# Revit family: Lavatory_System-Free_Standing-Trueform_Concrete-Single_Ramp_Basin-Configurable_2_Station
name_source: partatom
category: Plumbing Fixtures
revit_build: Autodesk Revit LT 2015 (Build: 20140606_1530(x64)
units: mm (PartAtom-declared; Revit-internal decimal feet)

## types (3) — shared parameters
Additional Support Required Note = No
Apron Height = 5"
Base = Steel, Paint Finish, Black, Matte
Basin Depth = 13"
Basin Front Setback = 4"
Basin Front Setback MAX = 7"
Basin Front Setback MIN = 3"
Basin Height = 5"
Basin/Countertop Reconciliation Warning = No
Countertop Height = 34"
Lavatory = GFRC - Concrete
Leveling Feet = Stainless Steel
Manufacturer = Trueform Concrete
Non Standard Sink Basin Model Note = No
Overall Countertop Depth = 22"
Overall Countertop Depth MIN = 18"
Tailpiece = Polished Chrome
URL = https://www.trueformconcrete.com
Vent Connection = No
Verify Basin Front Setback = 4"
Verify Overall Countertop Depth = 22"
Verify Rear Countertop = 5"
WFU = 3
Waste Connection = Yes
Waste Fitting = 1 1/2"

## per-type parameters (varying)
| type | Basin Center to Countertop Edge MIN | Basin Center to Left Countertop Edge | Basin Center to Right Countertop Edge | Basin ID (Do not edit value) | Basin Length | CWFU | Description | HWFU | LCC | Model | Overall Countertop Length | Overall Countertop Length MIN | RCC | SDC | Verify Basin Center to Left Countertop Edge | Verify Basin Center to Right Countertop Edge | Verify Overall Countertop Length |
| R-7213 | 41" | 45" | 45" | 7213 | 72" | 1.5 | Free-standing GFRC 2 or 3 Station Ramp Basin Lavatory | 1.5 | 45" | Custom Lavatory | 90" | 82" | 45" | 3/4" | 45" | 45" | 90" |
| R-4813 | 29" | 34" | 34" | 4813 | 48" | 1 | Free-standing GFRC 2 Station Ramp Basin Lavatory | 1 | 34" | ZEN-68-48V-ADA | 68" | 58" | 34" | 1/2" | 34" | 34" | 68" |
| R-6013 | 35" | 39" | 39" | 6013 | 60" | 1.5 | Free-standing GFRC 2 or 3 Station Ramp Basin Lavatory | 1.5 | 39" | Custom Lavatory | 78" | 70" | 39" | 5/8" | 39" | 39" | 78" |

## geometry (parser evidence)
native form markers: Sweep x4
no freeform markers — native parametric forms only
